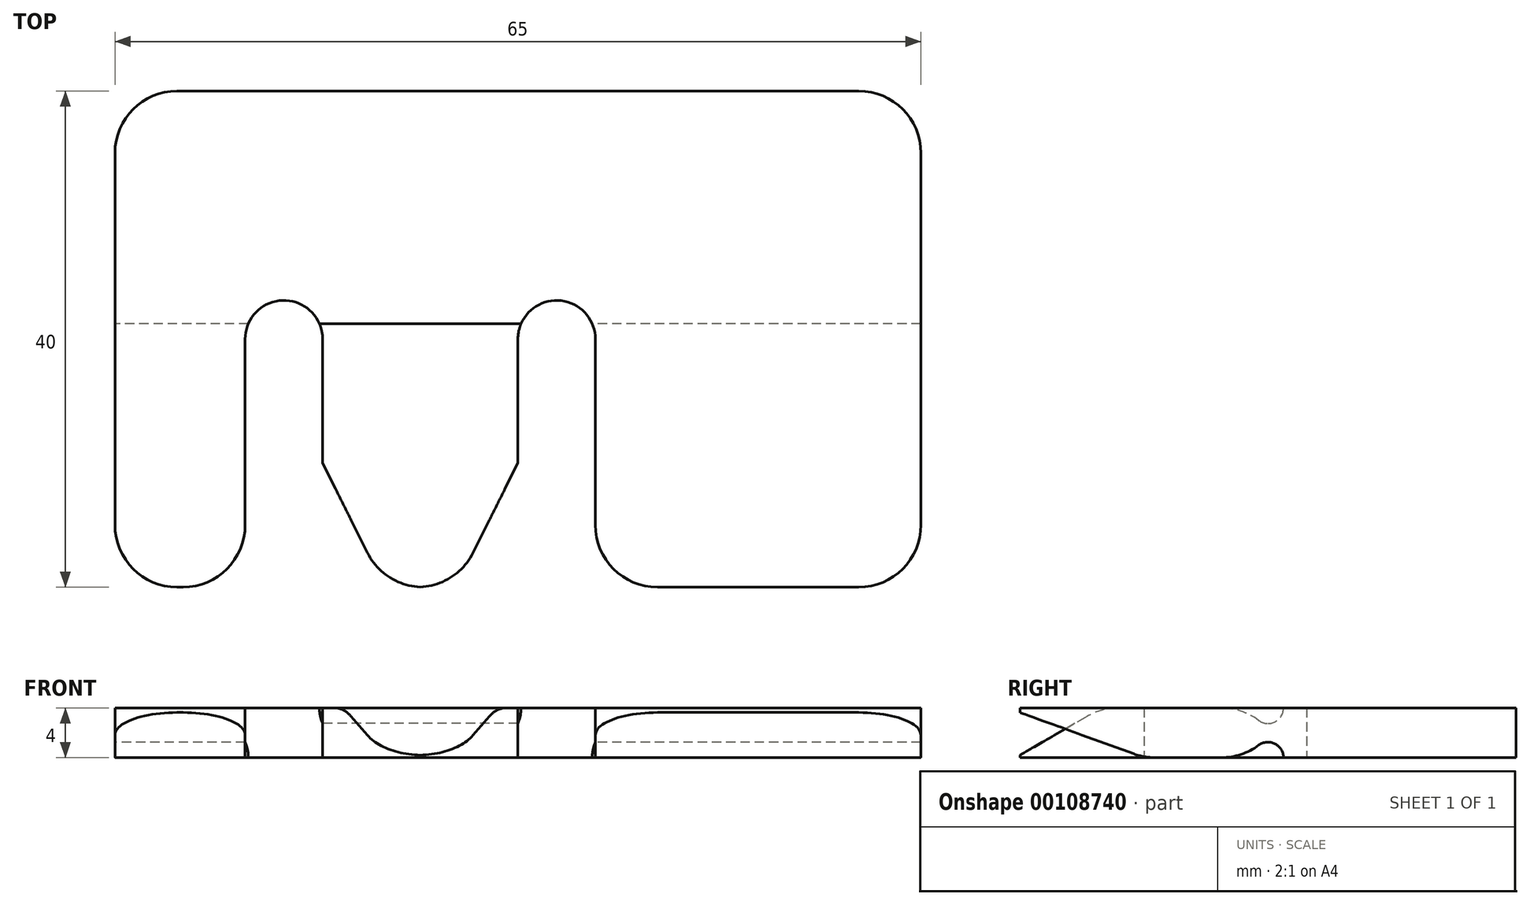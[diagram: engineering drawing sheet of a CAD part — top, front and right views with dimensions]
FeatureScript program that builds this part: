
annotation { "Feature Type Name" : "Feature", "Feature Type Description" : "" }
export const myFeature = defineFeature(function(context is Context, id is Id, definition is map)
    precondition{}
    {
        {
            var Q0;
            Q0=qCreatedBy(makeId("Top.planeOp"),FACE);
            var sketch = newSketch(context, id + "F0", { "sketchPlane" : qUnion([Q0])});
            skLineSegment(sketch, "E0.bottom", {"start": v(32.5, 20) * mm, "end": v(-32.5, 20) * mm});
            skLineSegment(sketch, "E0.top", {"start": v(32.5, -20) * mm, "end": v(-32.5, -20) * mm});
            skLineSegment(sketch, "E0.left", {"start": v(32.5, 20) * mm, "end": v(32.5, -20) * mm});
            skLineSegment(sketch, "E0.right", {"start": v(-32.5, 20) * mm, "end": v(-32.5, -20) * mm});
            skPoint(sketch, "E0.middle", {"position": v(0, 0) * mm});
            skLineSegment(sketch, "E1", {"start": v(-22, -20) * mm, "end": v(-22, 0) * mm});
            skLineSegment(sketch, "E2", {"start": v(-15.75, 0) * mm, "end": v(-15.75, -20) * mm});
            skLineSegment(sketch, "E3", {"start": v(0, 0) * mm, "end": v(0, -20) * mm});
            skLineSegment(sketch, "E4", {"start": v(6.25, 0) * mm, "end": v(6.25, -20) * mm});
            skCircle(sketch, "E5", {"center": v(-18.88, 0) * mm, "radius": 3.12 * mm});
            skCircle(sketch, "E6", {"center": v(3.12, 0) * mm, "radius": 3.12 * mm});
            skLineSegment(sketch, "E7", {"start": v(-15.75, -10) * mm, "end": v(-10.75, -20) * mm});
            skLineSegment(sketch, "E8", {"start": v(0, -10) * mm, "end": v(-5, -20) * mm});
            skSolve(sketch);
        }
        {
            var Q0;
            Q0=makeQuery(id+"F0.imprint","IMPRINT",FACE,{"disambiguationData":[TD([[makeQuery(id+"F0.imprint","IMPRINT",EDGE,{"derivedFrom":sQuery(id+"F0.wireOp",EDGE,"E0.bottom")}),1.0]])]});
            extrude(context, id + "F1", {"entities" : qUnion([Q0]), "depth" : 4 * mm});
        }
        {
            var Q0;
            Q0=makeQuery(id+"F1.opExtrude","SWEPT_FACE",FACE,{"disambiguationData":[OSD([sQuery(id+"F0.wireOp",EDGE,"E0.right")])]});
            var sketch = newSketch(context, id + "F2", { "sketchPlane" : qUnion([Q0])});
            skPoint(sketch, "E9.0", {"position": v(0, 0) * mm});
            skArc(sketch, "E10", {"start": v(1.25, 0) * mm, "mid": v(0, 1.25) * mm, "end": v(-1.25, 0) * mm});
            skLineSegment(sketch, "E11.0", {"start": v(-20, 0) * mm, "end": v(20, 0) * mm});
            skSolve(sketch);
        }
        {
            var Q0;
            Q0 = qSketchRegion(id + "F2", true);
            extrude(context, id + "F3", {"entities" : qUnion([Q0]), "operationType" : NewBodyOperationType.REMOVE, "endBound" : BoundingType.THROUGH_ALL, "oppositeDirection" : true, "depth" : 25 * mm});
        }
        {
            var Q0;
            Q0=makeQuery(id+"F0.imprint","IMPRINT",FACE,{"disambiguationData":[TD([[makeQuery(id+"F0.imprint","IMPRINT",EDGE,{"derivedFrom":sQuery(id+"F0.wireOp",EDGE,"E0.bottom")}),1.0]])]});
            var sketch = newSketch(context, id + "F4", { "sketchPlane" : qUnion([Q0])});
            skLineSegment(sketch, "E12.0", {"start": v(0.26, 1.25) * mm, "end": v(-16.01, 1.25) * mm});
            skLineSegment(sketch, "E13.0", {"start": v(0, -1.25) * mm, "end": v(-15.75, -1.25) * mm});
            skArc(sketch, "E14.0", {"start": v(-15.75, 0) * mm, "mid": v(-15.82, 0.64) * mm, "end": v(-16.01, 1.25) * mm});
            skLineSegment(sketch, "E15.0", {"start": v(-15.75, 0) * mm, "end": v(-15.75, -1.25) * mm});
            skArc(sketch, "E16.0", {"start": v(0.26, 1.25) * mm, "mid": v(0.07, 0.64) * mm, "end": v(0, 0) * mm});
            skLineSegment(sketch, "E17.0", {"start": v(0, 0) * mm, "end": v(0, -1.25) * mm});
            skSolve(sketch);
        }
        {
            var Q0;
            Q0 = qSketchRegion(id + "F4", true);
            extrude(context, id + "F5", {"entities" : qUnion([Q0]), "operationType" : NewBodyOperationType.ADD, "depth" : 2 * mm});
        }
        {
            var Q0;
            Q0=makeQuery(id+"F5.boolean.opBoolean","MERGE",FACE,{"derivedFrom":[makeQuery(id+"F1.opExtrude","SWEPT_FACE",FACE,{"disambiguationData":[OSD([sQuery(id+"F0.wireOp",EDGE,"E2")])]}),makeQuery(id+"F5.opExtrude","SWEPT_FACE",FACE,{"disambiguationData":[OSD([sQuery(id+"F4.wireOp",EDGE,"E15.0")])]})]});
            cPlane(context, id + "F6", {"entities" : qUnion([Q0]), "cplaneType" : CPlaneType.OFFSET, "offset" : 2 * mm, "width" : 150 * mm, "height" : 150 * mm});
        }
        {
            var Q0;
            Q0=qCreatedBy(id+"F6.planeOp",FACE);
            var sketch = newSketch(context, id + "F7", { "sketchPlane" : qUnion([Q0])});
            skPoint(sketch, "E18.0", {"position": v(0, 4) * mm});
            skLineSegment(sketch, "E19.0", {"start": v(0, 4) * mm, "end": v(10, 4) * mm});
            skLineSegment(sketch, "E20.0", {"start": v(-3.13, 4) * mm, "end": v(0, 4) * mm});
            skArc(sketch, "E21", {"start": v(-1.25, 4) * mm, "mid": v(0, 2.75) * mm, "end": v(1.25, 4) * mm});
            skSolve(sketch);
        }
        {
            var Q0;
            Q0 = qSketchRegion(id + "F7", true);
            extrude(context, id + "F8", {"entities" : qUnion([Q0]), "operationType" : NewBodyOperationType.REMOVE, "oppositeDirection" : true, "depth" : 20 * mm});
        }
        {
            var Q0;
            {var subQ0=sQuery(id+"F0.wireOp",EDGE,"E0.top");Q0=makeQuery(id+"F1.opExtrude","CAP_EDGE",EDGE,{"disambiguationData":[OSD([subQ0]),TDD([makeQuery(id+"F0.imprint","IMPRINT",EDGE,{"disambiguationData":[TD([[makeQuery(id+"F0.imprint","INTERSECT",VERTEX,{"derivedFrom":[subQ0,sQuery(id+"F0.wireOp",EDGE,"E7")]}),1.0]])],"derivedFrom":subQ0})])],"isStart":false});}
            chamfer(context, id + "F9", {"entities" : qUnion([Q0]), "chamferType" : ChamferType.OFFSET_ANGLE, "width" : 3.8 * mm, "oppositeDirection" : false, "angle" : 60 * degree, "tangentPropagation" : true});
        }
        {
            var Q0;
            {var subQ0=sQuery(id+"F0.wireOp",EDGE,"E0.top");Q0=makeQuery(id+"F1.opExtrude","CAP_EDGE",EDGE,{"disambiguationData":[OSD([subQ0]),TDD([makeQuery(id+"F0.imprint","IMPRINT",EDGE,{"disambiguationData":[TD([[makeQuery(id+"F0.imprint","INTERSECT",VERTEX,{"derivedFrom":[subQ0,sQuery(id+"F0.wireOp",EDGE,"E0.right")]}),1.0]])],"derivedFrom":subQ0})])],"isStart":true});}
            var Q1;
            {var subQ0=sQuery(id+"F0.wireOp",EDGE,"E0.top");Q1=makeQuery(id+"F1.opExtrude","CAP_EDGE",EDGE,{"disambiguationData":[OSD([subQ0]),TDD([makeQuery(id+"F0.imprint","IMPRINT",EDGE,{"disambiguationData":[TD([[makeQuery(id+"F0.imprint","INTERSECT",VERTEX,{"derivedFrom":[subQ0,sQuery(id+"F0.wireOp",EDGE,"E0.left")]}),-1.0]])],"derivedFrom":subQ0})])],"isStart":true});}
            chamfer(context, id + "F10", {"entities" : qUnion([Q0, Q1]), "chamferType" : ChamferType.OFFSET_ANGLE, "width" : 10 * mm, "oppositeDirection" : false, "angle" : 20 * degree, "tangentPropagation" : true});
        }
        {
            var Q0;
            {var subQ0=sQuery(id+"F0.wireOp",EDGE,"E7");var subQ1=sQuery(id+"F0.wireOp",EDGE,"E3");var subQ2=sQuery(id+"F0.wireOp",EDGE,"E2");var subQ3=sQuery(id+"F0.wireOp",EDGE,"E0.top");var subQ4=sQuery(id+"F0.wireOp",EDGE,"E8");var subQ5=makeQuery(id+"F0.imprint","IMPRINT",EDGE,{"disambiguationData":[TD([[makeQuery(id+"F0.imprint","INTERSECT",VERTEX,{"derivedFrom":[subQ3,subQ0]}),1.0]])],"derivedFrom":subQ3});Q0=makeQuery(id+"F9.opChamfer","BLEND_EDGE",EDGE,{"blendedFrom":[makeQuery(id+"F1.opExtrude","CAP_EDGE",EDGE,{"disambiguationData":[OSD([subQ3]),TDD([subQ5])],"isStart":false}),makeQuery(id+"F8.boolean.opBoolean","SPLIT",FACE,{"disambiguationData":[TD([makeQuery(id+"F1.opExtrude","SWEPT_FACE",FACE,{"disambiguationData":[OSD([subQ2])]})])],"derivedFrom":makeQuery(id+"F1.opExtrude","CAP_FACE",FACE,{"disambiguationData":[OSD([sQuery(id+"F0.wireOp",EDGE,"E0.bottom"),subQ3,sQuery(id+"F0.wireOp",EDGE,"E0.left"),sQuery(id+"F0.wireOp",EDGE,"E0.right"),sQuery(id+"F0.wireOp",EDGE,"E1"),subQ2,subQ1,sQuery(id+"F0.wireOp",EDGE,"E4"),sQuery(id+"F0.wireOp",EDGE,"E5"),sQuery(id+"F0.wireOp",EDGE,"E6"),subQ0,subQ4])],"isStart":false})})],"blendedInto":[makeQuery(id+"F8.boolean.opBoolean","SPLIT",FACE,{"disambiguationData":[TD([makeQuery(id+"F1.opExtrude","SWEPT_FACE",FACE,{"disambiguationData":[OSD([subQ2])]})])],"derivedFrom":makeQuery(id+"F1.opExtrude","CAP_FACE",FACE,{"disambiguationData":[OSD([sQuery(id+"F0.wireOp",EDGE,"E0.bottom"),subQ3,sQuery(id+"F0.wireOp",EDGE,"E0.left"),sQuery(id+"F0.wireOp",EDGE,"E0.right"),sQuery(id+"F0.wireOp",EDGE,"E1"),subQ2,subQ1,sQuery(id+"F0.wireOp",EDGE,"E4"),sQuery(id+"F0.wireOp",EDGE,"E5"),sQuery(id+"F0.wireOp",EDGE,"E6"),subQ0,subQ4])],"isStart":false})})]});}
            var Q1;
            {var subQ0=sQuery(id+"F0.wireOp",EDGE,"E0.right");var subQ1=sQuery(id+"F0.wireOp",EDGE,"E0.top");var subQ2=sQuery(id+"F0.wireOp",EDGE,"E1");var subQ3=makeQuery(id+"F0.imprint","IMPRINT",EDGE,{"disambiguationData":[TD([[makeQuery(id+"F0.imprint","INTERSECT",VERTEX,{"derivedFrom":[subQ1,subQ0]}),1.0]])],"derivedFrom":subQ1});Q1=makeQuery(id+"F10.opChamfer","BLEND_EDGE",EDGE,{"blendedFrom":[makeQuery(id+"F1.opExtrude","CAP_EDGE",EDGE,{"disambiguationData":[OSD([subQ1]),TDD([subQ3])],"isStart":true}),makeQuery(id+"F3.boolean.opBoolean","SPLIT",FACE,{"disambiguationData":[TD([makeQuery(id+"F1.opExtrude","SWEPT_FACE",FACE,{"disambiguationData":[OSD([subQ2])]})])],"derivedFrom":makeQuery(id+"F1.opExtrude","CAP_FACE",FACE,{"disambiguationData":[OSD([sQuery(id+"F0.wireOp",EDGE,"E0.bottom"),subQ1,sQuery(id+"F0.wireOp",EDGE,"E0.left"),subQ0,subQ2,sQuery(id+"F0.wireOp",EDGE,"E2"),sQuery(id+"F0.wireOp",EDGE,"E3"),sQuery(id+"F0.wireOp",EDGE,"E4"),sQuery(id+"F0.wireOp",EDGE,"E5"),sQuery(id+"F0.wireOp",EDGE,"E6"),sQuery(id+"F0.wireOp",EDGE,"E7"),sQuery(id+"F0.wireOp",EDGE,"E8")])],"isStart":true})})],"blendedInto":[makeQuery(id+"F3.boolean.opBoolean","SPLIT",FACE,{"disambiguationData":[TD([makeQuery(id+"F1.opExtrude","SWEPT_FACE",FACE,{"disambiguationData":[OSD([subQ2])]})])],"derivedFrom":makeQuery(id+"F1.opExtrude","CAP_FACE",FACE,{"disambiguationData":[OSD([sQuery(id+"F0.wireOp",EDGE,"E0.bottom"),subQ1,sQuery(id+"F0.wireOp",EDGE,"E0.left"),subQ0,subQ2,sQuery(id+"F0.wireOp",EDGE,"E2"),sQuery(id+"F0.wireOp",EDGE,"E3"),sQuery(id+"F0.wireOp",EDGE,"E4"),sQuery(id+"F0.wireOp",EDGE,"E5"),sQuery(id+"F0.wireOp",EDGE,"E6"),sQuery(id+"F0.wireOp",EDGE,"E7"),sQuery(id+"F0.wireOp",EDGE,"E8")])],"isStart":true})})]});}
            var Q2;
            {var subQ0=sQuery(id+"F0.wireOp",EDGE,"E0.left");var subQ1=sQuery(id+"F0.wireOp",EDGE,"E0.top");var subQ2=sQuery(id+"F0.wireOp",EDGE,"E4");var subQ3=makeQuery(id+"F0.imprint","IMPRINT",EDGE,{"disambiguationData":[TD([[makeQuery(id+"F0.imprint","INTERSECT",VERTEX,{"derivedFrom":[subQ1,subQ0]}),-1.0]])],"derivedFrom":subQ1});Q2=makeQuery(id+"F10.opChamfer","BLEND_EDGE",EDGE,{"blendedFrom":[makeQuery(id+"F1.opExtrude","CAP_EDGE",EDGE,{"disambiguationData":[OSD([subQ1]),TDD([subQ3])],"isStart":true}),makeQuery(id+"F3.boolean.opBoolean","SPLIT",FACE,{"disambiguationData":[TD([makeQuery(id+"F1.opExtrude","SWEPT_FACE",FACE,{"disambiguationData":[OSD([subQ2])]})])],"derivedFrom":makeQuery(id+"F1.opExtrude","CAP_FACE",FACE,{"disambiguationData":[OSD([sQuery(id+"F0.wireOp",EDGE,"E0.bottom"),subQ1,subQ0,sQuery(id+"F0.wireOp",EDGE,"E0.right"),sQuery(id+"F0.wireOp",EDGE,"E1"),sQuery(id+"F0.wireOp",EDGE,"E2"),sQuery(id+"F0.wireOp",EDGE,"E3"),subQ2,sQuery(id+"F0.wireOp",EDGE,"E5"),sQuery(id+"F0.wireOp",EDGE,"E6"),sQuery(id+"F0.wireOp",EDGE,"E7"),sQuery(id+"F0.wireOp",EDGE,"E8")])],"isStart":true})})],"blendedInto":[makeQuery(id+"F3.boolean.opBoolean","SPLIT",FACE,{"disambiguationData":[TD([makeQuery(id+"F1.opExtrude","SWEPT_FACE",FACE,{"disambiguationData":[OSD([subQ2])]})])],"derivedFrom":makeQuery(id+"F1.opExtrude","CAP_FACE",FACE,{"disambiguationData":[OSD([sQuery(id+"F0.wireOp",EDGE,"E0.bottom"),subQ1,subQ0,sQuery(id+"F0.wireOp",EDGE,"E0.right"),sQuery(id+"F0.wireOp",EDGE,"E1"),sQuery(id+"F0.wireOp",EDGE,"E2"),sQuery(id+"F0.wireOp",EDGE,"E3"),subQ2,sQuery(id+"F0.wireOp",EDGE,"E5"),sQuery(id+"F0.wireOp",EDGE,"E6"),sQuery(id+"F0.wireOp",EDGE,"E7"),sQuery(id+"F0.wireOp",EDGE,"E8")])],"isStart":true})})]});}
            var Q3;
            {var subQ0=sQuery(id+"F2.wireOp",EDGE,"E11.0");var subQ1=sQuery(id+"F2.wireOp",EDGE,"E10");Q3=makeQuery(id+"F3.boolean.opBoolean","COPY",EDGE,{"disambiguationData":[OD(0.0)],"derivedFrom":makeQuery(id+"F3.opExtrude","SWEPT_EDGE",EDGE,{"disambiguationData":[OSD([subQ1,subQ0]),TDD([makeQuery(id+"F2.imprint","INTERSECT",VERTEX,{"disambiguationData":[OD(0.0)],"derivedFrom":[subQ1,subQ0]})])]})});}
            var Q4;
            {var subQ0=sQuery(id+"F2.wireOp",EDGE,"E11.0");var subQ1=sQuery(id+"F2.wireOp",EDGE,"E10");Q4=makeQuery(id+"F3.boolean.opBoolean","COPY",EDGE,{"disambiguationData":[OD(2.0)],"derivedFrom":makeQuery(id+"F3.opExtrude","SWEPT_EDGE",EDGE,{"disambiguationData":[OSD([subQ1,subQ0]),TDD([makeQuery(id+"F2.imprint","INTERSECT",VERTEX,{"disambiguationData":[OD(0.0)],"derivedFrom":[subQ1,subQ0]})])]})});}
            var Q5;
            Q5=makeQuery(id+"F8.boolean.opBoolean","COPY",EDGE,{"derivedFrom":makeQuery(id+"F8.opExtrude","SWEPT_EDGE",EDGE,{"disambiguationData":[OSD([sQuery(id+"F7.wireOp",EDGE,"E19.0"),sQuery(id+"F7.wireOp",EDGE,"E21")])]})});
            var Q6;
            Q6=makeQuery(id+"F1.opExtrude","SWEPT_EDGE",EDGE,{"disambiguationData":[OSD([sQuery(id+"F0.wireOp",EDGE,"E0.bottom"),sQuery(id+"F0.wireOp",EDGE,"E0.right")])]});
            var Q7;
            Q7=makeQuery(id+"F1.opExtrude","SWEPT_EDGE",EDGE,{"disambiguationData":[OSD([sQuery(id+"F0.wireOp",EDGE,"E0.bottom"),sQuery(id+"F0.wireOp",EDGE,"E0.left")])]});
            var Q8;
            Q8=makeQuery(id+"F1.opExtrude","SWEPT_EDGE",EDGE,{"disambiguationData":[OSD([sQuery(id+"F0.wireOp",EDGE,"E0.top"),sQuery(id+"F0.wireOp",EDGE,"E0.right")])]});
            var Q9;
            Q9=makeQuery(id+"F1.opExtrude","SWEPT_EDGE",EDGE,{"disambiguationData":[OSD([sQuery(id+"F0.wireOp",EDGE,"E0.top"),sQuery(id+"F0.wireOp",EDGE,"E1")])]});
            var Q10;
            Q10=makeQuery(id+"F1.opExtrude","SWEPT_EDGE",EDGE,{"disambiguationData":[OSD([sQuery(id+"F0.wireOp",EDGE,"E0.top"),sQuery(id+"F0.wireOp",EDGE,"E4")])]});
            var Q11;
            Q11=makeQuery(id+"F1.opExtrude","SWEPT_EDGE",EDGE,{"disambiguationData":[OSD([sQuery(id+"F0.wireOp",EDGE,"E0.top"),sQuery(id+"F0.wireOp",EDGE,"E0.left")])]});
            var Q12;
            Q12=makeQuery(id+"F1.opExtrude","SWEPT_EDGE",EDGE,{"disambiguationData":[OSD([sQuery(id+"F0.wireOp",EDGE,"E0.top"),sQuery(id+"F0.wireOp",EDGE,"E8")])]});
            var Q13;
            Q13=makeQuery(id+"F1.opExtrude","SWEPT_EDGE",EDGE,{"disambiguationData":[OSD([sQuery(id+"F0.wireOp",EDGE,"E0.top"),sQuery(id+"F0.wireOp",EDGE,"E7")])]});
            fillet(context, id + "F11", {"entities" : qUnion([Q0, Q1, Q2, Q3, Q4, Q5, Q6, Q7, Q8, Q9, Q10, Q11, Q12, Q13]), "radius" : 5 * mm, "tangentPropagation" : true, "allowEdgeOverflow" : false});
        }
    });
